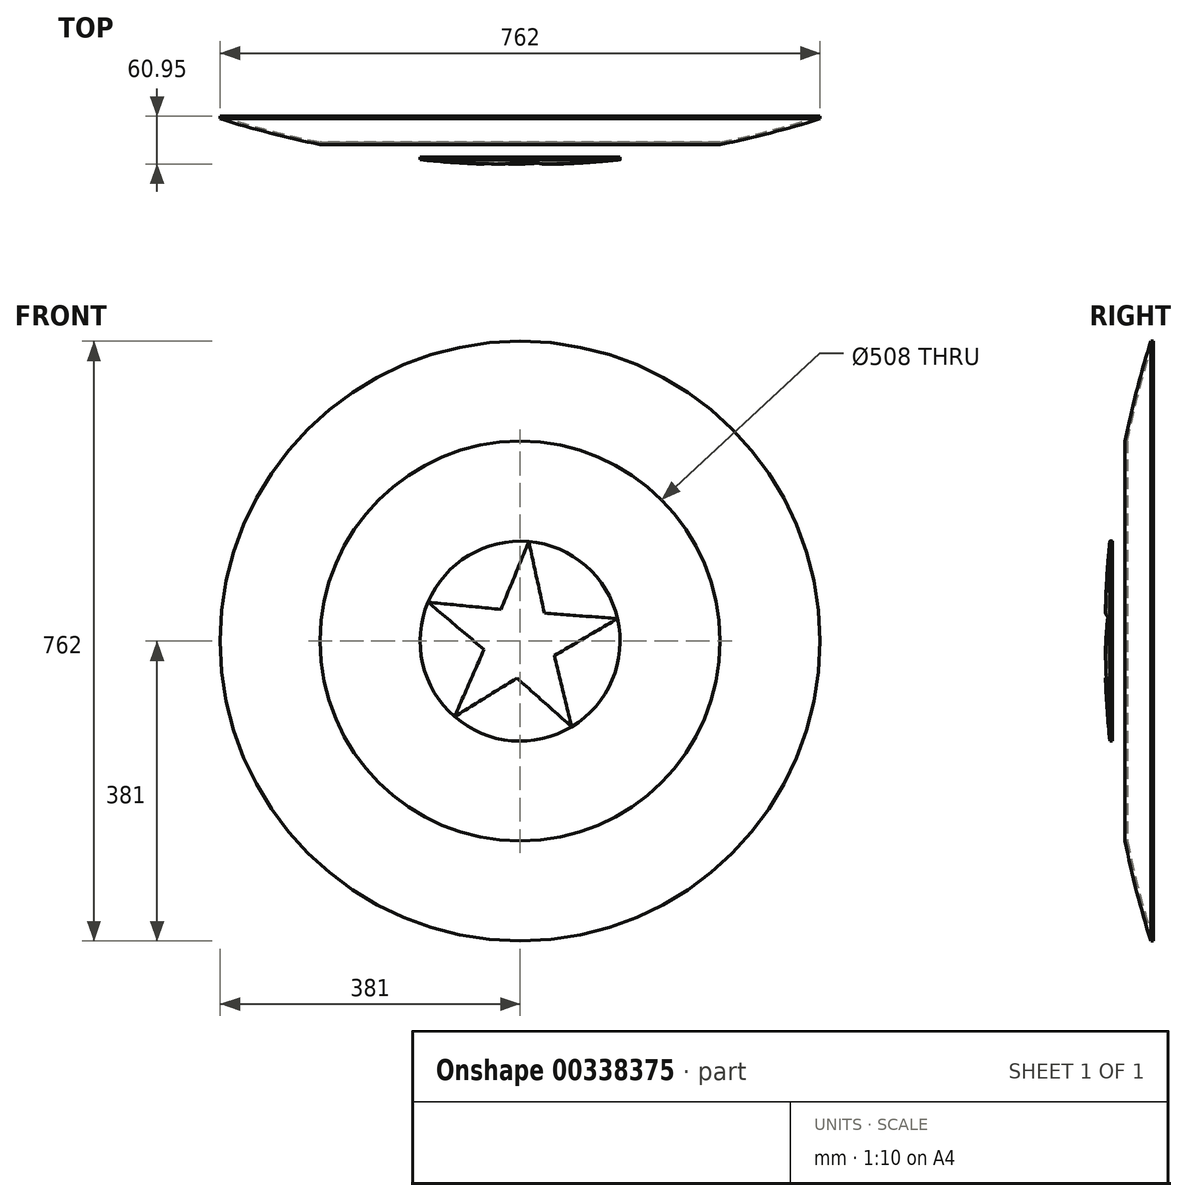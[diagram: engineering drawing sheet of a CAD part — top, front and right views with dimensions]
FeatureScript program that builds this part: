
annotation { "Feature Type Name" : "Feature", "Feature Type Description" : "" }
export const myFeature = defineFeature(function(context is Context, id is Id, definition is map)
    precondition{}
    {
        {
            var Q0;
            Q0=qCreatedBy(makeId("Top.planeOp"),FACE);
            var sketch = newSketch(context, id + "F0", { "sketchPlane" : qUnion([Q0])});
            skCircle(sketch, "E0", {"center": v(0, 1266.83) * mm, "radius": 1270 * mm});
            skCircle(sketch, "E1", {"center": v(0, 1266.83) * mm, "radius": 1263.65 * mm});
            skLineSegment(sketch, "E2", {"start": v(0, 3.17) * mm, "end": v(0, -3.17) * mm});
            skPoint(sketch, "E3", {"position": v(-508, 12.48) * mm});
            skLineSegment(sketch, "E4", {"start": v(-508, 12.48) * mm, "end": v(-508, 102.85) * mm});
            skLineSegment(sketch, "E5", {"start": v(-508, 102.85) * mm, "end": v(508, 102.85) * mm});
            skPoint(sketch, "E6", {"position": v(-177.8, -235.44) * mm});
            skPoint(sketch, "E7", {"position": v(-359.25, -218.64) * mm});
            skPoint(sketch, "E8", {"position": v(254, 10.57) * mm});
            skPoint(sketch, "E9", {"position": v(381, 38.32) * mm});
            skPoint(sketch, "E10.start.orphan", {"position": v(0, 0) * mm});
            skCircle(sketch, "E11", {"center": v(0, 1266.83) * mm, "radius": 1266.83 * mm});
            skPoint(sketch, "E12.start.orphan", {"position": v(127, 0) * mm});
            skLineSegment(sketch, "E13", {"start": v(381, 38.32) * mm, "end": v(381, 58.65) * mm});
            skLineSegment(sketch, "E14", {"start": v(254, 10.57) * mm, "end": v(254, 25.72) * mm});
            skLineSegment(sketch, "E15", {"start": v(127, 0) * mm, "end": v(127, 6.38) * mm});
            skSolve(sketch);
        }
        {
            var Q0;
            {var subQ0=sQuery(id+"F0.wireOp",EDGE,"E14");var subQ1=sQuery(id+"F0.wireOp",EDGE,"E0");var subQ2=makeQuery(id+"F0.imprint","INTERSECT",VERTEX,{"derivedFrom":[subQ1,subQ0]});Q0=makeQuery(id+"F0.imprint","IMPRINT",FACE,{"disambiguationData":[TD([[makeQuery(id+"F0.imprint","IMPRINT",EDGE,{"disambiguationData":[TD([[subQ2,-1.0]])],"derivedFrom":subQ1}),1.0]])]});}
            var Q1;
            {var subQ0=sQuery(id+"F0.wireOp",EDGE,"E2");var subQ1=sQuery(id+"F0.wireOp",EDGE,"E0");var subQ2=makeQuery(id+"F0.imprint","INTERSECT",VERTEX,{"derivedFrom":[subQ1,subQ0]});Q1=makeQuery(id+"F0.imprint","IMPRINT",FACE,{"disambiguationData":[TD([[makeQuery(id+"F0.imprint","IMPRINT",EDGE,{"disambiguationData":[TD([[subQ2,-1.0]])],"derivedFrom":subQ1}),1.0]])]});}
            var Q2;
            Q2=sQuery(id+"F0.wireOp",EDGE,"E2");
            revolve(context, id + "F1", {"entities" : qUnion([Q0, Q1]), "axis" : qUnion([Q2]), "revolveType" : RevolveType.FULL});
        }
        {
            var Q0;
            Q0=qCreatedBy(makeId("Front.planeOp"),FACE);
            cPlane(context, id + "F2", {"entities" : qUnion([Q0]), "cplaneType" : CPlaneType.OFFSET, "offset" : 25.4 * mm, "width" : 152.4 * mm, "height" : 152.4 * mm});
        }
        {
            var Q0;
            Q0=qCreatedBy(id+"F2.planeOp",FACE);
            var sketch = newSketch(context, id + "F3", { "sketchPlane" : qUnion([Q0])});
            skPoint(sketch, "E16", {"position": v(0, 0) * mm});
            skCircle(sketch, "E17", {"center": v(0, 0) * mm, "radius": 127 * mm});
            skCircle(sketch, "E18.cCircle", {"center": v(0, 0) * mm, "radius": 38.1 * mm, "construction": true});
            skLineSegment(sketch, "E18.0", {"start": v(-45.88, -10.63) * mm, "end": v(-24.28, 40.35) * mm});
            skLineSegment(sketch, "E18.1", {"start": v(-24.28, 40.35) * mm, "end": v(30.87, 35.56) * mm});
            skLineSegment(sketch, "E18.2", {"start": v(30.87, 35.56) * mm, "end": v(43.36, -18.37) * mm});
            skLineSegment(sketch, "E18.3", {"start": v(43.36, -18.37) * mm, "end": v(-4.07, -46.92) * mm});
            skLineSegment(sketch, "E18.4", {"start": v(-4.07, -46.92) * mm, "end": v(-45.88, -10.63) * mm});
            skPoint(sketch, "E18.0.midPoint", {"position": v(-35.08, 14.86) * mm});
            skLineSegment(sketch, "E19", {"start": v(-24.98, -28.77) * mm, "end": v(-83.25, -95.9) * mm});
            skLineSegment(sketch, "E20", {"start": v(-83.25, -95.9) * mm, "end": v(-45.88, -10.63) * mm});
            skLineSegment(sketch, "E21", {"start": v(-4.07, -46.92) * mm, "end": v(-83.25, -95.9) * mm});
            skLineSegment(sketch, "E22", {"start": v(19.65, -32.64) * mm, "end": v(65.49, -108.81) * mm});
            skLineSegment(sketch, "E23", {"start": v(65.49, -108.81) * mm, "end": v(43.36, -18.37) * mm});
            skLineSegment(sketch, "E24", {"start": v(-4.07, -46.92) * mm, "end": v(65.49, -108.81) * mm});
            skLineSegment(sketch, "E25", {"start": v(-35.08, 14.86) * mm, "end": v(-116.94, 49.54) * mm});
            skLineSegment(sketch, "E26", {"start": v(-116.94, 49.54) * mm, "end": v(-45.88, -10.63) * mm});
            skLineSegment(sketch, "E27", {"start": v(-24.28, 40.35) * mm, "end": v(-116.94, 49.54) * mm});
            skLineSegment(sketch, "E28", {"start": v(37.12, 8.6) * mm, "end": v(123.72, 28.66) * mm});
            skLineSegment(sketch, "E29", {"start": v(123.72, 28.66) * mm, "end": v(30.87, 35.56) * mm});
            skLineSegment(sketch, "E30", {"start": v(43.36, -18.37) * mm, "end": v(123.72, 28.66) * mm});
            skLineSegment(sketch, "E31", {"start": v(3.3, 37.96) * mm, "end": v(10.98, 126.52) * mm});
            skLineSegment(sketch, "E32", {"start": v(10.98, 126.52) * mm, "end": v(-24.28, 40.35) * mm});
            skLineSegment(sketch, "E33", {"start": v(30.87, 35.56) * mm, "end": v(10.98, 126.52) * mm});
            skSolve(sketch);
        }
        {
            var Q0;
            {var subQ4=sQuery(id+"F3.wireOp",EDGE,"E18.0");var subQ6=makeQuery(id+"F3.imprint","INTERSECT",VERTEX,{"derivedFrom":[subQ4,sQuery(id+"F3.wireOp",EDGE,"E25")]});Q0=makeQuery(id+"F3.imprint","IMPRINT",FACE,{"disambiguationData":[TD([[makeQuery(id+"F3.imprint","IMPRINT",EDGE,{"disambiguationData":[TD([[subQ6,1.0]])],"derivedFrom":subQ4}),-1.0]])]});}
            var Q1;
            {var subQ2=sQuery(id+"F3.wireOp",EDGE,"E31");Q1=makeQuery(id+"F3.imprint","IMPRINT",FACE,{"disambiguationData":[TD([[makeQuery(id+"F3.imprint","IMPRINT",EDGE,{"derivedFrom":subQ2}),-1.0]])]});}
            var Q2;
            {var subQ2=sQuery(id+"F3.wireOp",EDGE,"E31");Q2=makeQuery(id+"F3.imprint","IMPRINT",FACE,{"disambiguationData":[TD([[makeQuery(id+"F3.imprint","IMPRINT",EDGE,{"derivedFrom":subQ2}),1.0]])]});}
            var Q3;
            {var subQ2=sQuery(id+"F3.wireOp",EDGE,"E25");Q3=makeQuery(id+"F3.imprint","IMPRINT",FACE,{"disambiguationData":[TD([[makeQuery(id+"F3.imprint","IMPRINT",EDGE,{"derivedFrom":subQ2}),-1.0]])]});}
            var Q4;
            {var subQ2=sQuery(id+"F3.wireOp",EDGE,"E25");Q4=makeQuery(id+"F3.imprint","IMPRINT",FACE,{"disambiguationData":[TD([[makeQuery(id+"F3.imprint","IMPRINT",EDGE,{"derivedFrom":subQ2}),1.0]])]});}
            var Q5;
            {var subQ2=sQuery(id+"F3.wireOp",EDGE,"E19");Q5=makeQuery(id+"F3.imprint","IMPRINT",FACE,{"disambiguationData":[TD([[makeQuery(id+"F3.imprint","IMPRINT",EDGE,{"derivedFrom":subQ2}),-1.0]])]});}
            var Q6;
            {var subQ2=sQuery(id+"F3.wireOp",EDGE,"E19");Q6=makeQuery(id+"F3.imprint","IMPRINT",FACE,{"disambiguationData":[TD([[makeQuery(id+"F3.imprint","IMPRINT",EDGE,{"derivedFrom":subQ2}),1.0]])]});}
            var Q7;
            {var subQ2=sQuery(id+"F3.wireOp",EDGE,"E22");Q7=makeQuery(id+"F3.imprint","IMPRINT",FACE,{"disambiguationData":[TD([[makeQuery(id+"F3.imprint","IMPRINT",EDGE,{"derivedFrom":subQ2}),1.0]])]});}
            var Q8;
            {var subQ2=sQuery(id+"F3.wireOp",EDGE,"E22");Q8=makeQuery(id+"F3.imprint","IMPRINT",FACE,{"disambiguationData":[TD([[makeQuery(id+"F3.imprint","IMPRINT",EDGE,{"derivedFrom":subQ2}),-1.0]])]});}
            var Q9;
            {var subQ2=sQuery(id+"F3.wireOp",EDGE,"E28");Q9=makeQuery(id+"F3.imprint","IMPRINT",FACE,{"disambiguationData":[TD([[makeQuery(id+"F3.imprint","IMPRINT",EDGE,{"derivedFrom":subQ2}),1.0]])]});}
            var Q10;
            {var subQ2=sQuery(id+"F3.wireOp",EDGE,"E28");Q10=makeQuery(id+"F3.imprint","IMPRINT",FACE,{"disambiguationData":[TD([[makeQuery(id+"F3.imprint","IMPRINT",EDGE,{"derivedFrom":subQ2}),-1.0]])]});}
            extrude(context, id + "F4", {"entities" : qUnion([Q0, Q1, Q2, Q3, Q4, Q5, Q6, Q7, Q8, Q9, Q10]), "operationType" : NewBodyOperationType.REMOVE, "endBound" : BoundingType.THROUGH_ALL, "oppositeDirection" : true, "depth" : 25.4 * mm});
        }
    });
